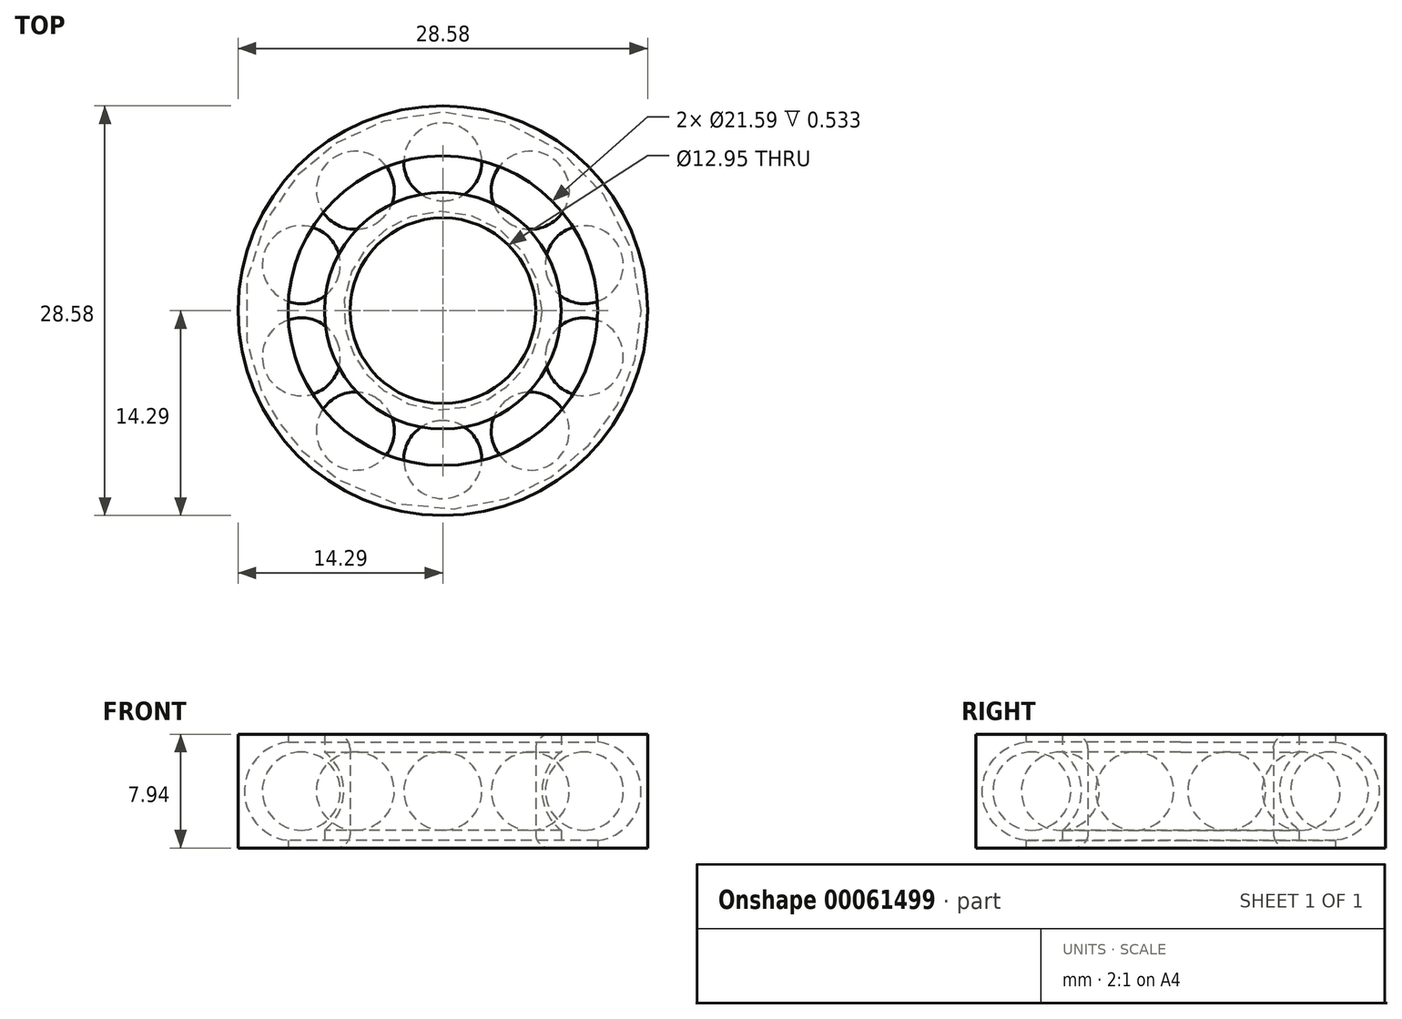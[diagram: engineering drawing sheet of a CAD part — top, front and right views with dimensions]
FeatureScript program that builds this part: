
annotation { "Feature Type Name" : "Feature", "Feature Type Description" : "" }
export const myFeature = defineFeature(function(context is Context, id is Id, definition is map)
    precondition{}
    {
        {
            var Q0;
            Q0=qCreatedBy(makeId("Top.planeOp"),FACE);
            var sketch = newSketch(context, id + "F0", { "sketchPlane" : qUnion([Q0])});
            skCircle(sketch, "E0", {"center": v(0, 0) * mm, "radius": 6.48 * mm});
            skCircle(sketch, "E1", {"center": v(0, 0) * mm, "radius": 14.29 * mm});
            skSolve(sketch);
        }
        {
            var Q0;
            Q0 = qSketchRegion(id + "F0", true);
            extrude(context, id + "F1", {"entities" : qUnion([Q0]), "depth" : 7.94 * mm});
        }
        {
            var Q0;
            Q0=qCreatedBy(makeId("Top.planeOp"),FACE);
            var sketch = newSketch(context, id + "F2", { "sketchPlane" : qUnion([Q0])});
            skCircle(sketch, "E2", {"center": v(0, 0) * mm, "radius": 8.26 * mm});
            skCircle(sketch, "E3", {"center": v(0, 0) * mm, "radius": 10.8 * mm});
            skSolve(sketch);
        }
        {
            var Q0;
            Q0 = qSketchRegion(id + "F2", true);
            extrude(context, id + "F3", {"entities" : qUnion([Q0]), "operationType" : NewBodyOperationType.REMOVE, "endBound" : BoundingType.UP_TO_NEXT, "depth" : 6 * mm});
        }
        {
            var Q0;
            Q0=qCreatedBy(makeId("Right.planeOp"),FACE);
            var sketch = newSketch(context, id + "F4", { "sketchPlane" : qUnion([Q0])});
            skLineSegment(sketch, "E4", {"start": v(10.38, 3.97) * mm, "end": v(10.38, 7.94) * mm, "construction": true});
            skLineSegment(sketch, "E5.0", {"start": v(-6.48, 7.94) * mm, "end": v(6.48, 7.94) * mm, "construction": true});
            skLineSegment(sketch, "E5.1", {"start": v(-14.29, 7.94) * mm, "end": v(14.29, 7.94) * mm, "construction": true});
            skLineSegment(sketch, "E6", {"start": v(6.48, 7.94) * mm, "end": v(14.29, 7.94) * mm, "construction": true});
            skLineSegment(sketch, "E7", {"start": v(14.29, 7.94) * mm, "end": v(14.29, 0) * mm, "construction": true});
            skLineSegment(sketch, "E8", {"start": v(6.48, 7.94) * mm, "end": v(6.48, 0) * mm, "construction": true});
            skLineSegment(sketch, "E9", {"start": v(6.48, 3.97) * mm, "end": v(14.29, 3.97) * mm, "construction": true});
            skLineSegment(sketch, "E10", {"start": v(0, 0) * mm, "end": v(0, 7.94) * mm, "construction": true});
            skCircle(sketch, "E11", {"center": v(10.38, 3.97) * mm, "radius": 3.46 * mm});
            skSolve(sketch);
        }
        {
            var Q0;
            Q0=makeQuery(id+"F4.imprint","IMPRINT",FACE,{"disambiguationData":[TD([[makeQuery(id+"F4.imprint","IMPRINT",EDGE,{"derivedFrom":sQuery(id+"F4.wireOp",EDGE,"E11")}),1.0]])]});
            var Q1;
            Q1=sQuery(id+"F4.wireOp",EDGE,"E10");
            revolve(context, id + "F5", {"operationType" : NewBodyOperationType.REMOVE, "entities" : qUnion([Q0]), "axis" : qUnion([Q1]), "revolveType" : RevolveType.FULL, "oppositeDirection" : true});
        }
        {
            var Q0;
            Q0=qCreatedBy(makeId("Right.planeOp"),FACE);
            var sketch = newSketch(context, id + "F6", { "sketchPlane" : qUnion([Q0])});
            skLineSegment(sketch, "E12.0", {"start": v(-14.29, 7.94) * mm, "end": v(14.29, 7.94) * mm, "construction": true});
            skLineSegment(sketch, "E13", {"start": v(0, 0) * mm, "end": v(0, 7.94) * mm, "construction": true});
            skLineSegment(sketch, "E14.0", {"start": v(-6.48, 7.94) * mm, "end": v(6.48, 7.94) * mm, "construction": true});
            skLineSegment(sketch, "E15", {"start": v(6.48, 7.94) * mm, "end": v(14.29, 7.94) * mm, "construction": true});
            skLineSegment(sketch, "E16", {"start": v(6.48, 7.94) * mm, "end": v(6.48, 0) * mm, "construction": true});
            skLineSegment(sketch, "E17", {"start": v(14.29, 7.94) * mm, "end": v(14.29, 0) * mm, "construction": true});
            skLineSegment(sketch, "E18", {"start": v(10.38, 7.94) * mm, "end": v(10.38, 0) * mm, "construction": true});
            skArc(sketch, "E19", {"start": v(10.38, 6.7) * mm, "mid": v(7.66, 3.97) * mm, "end": v(10.38, 1.25) * mm});
            skLineSegment(sketch, "E20", {"start": v(10.38, 6.7) * mm, "end": v(10.38, 1.25) * mm});
            skSolve(sketch);
        }
        {
            var Q0;
            Q0 = qSketchRegion(id + "F6", true);
            var Q1;
            Q1=sQuery(id+"F4.wireOp",EDGE,"E4");
            revolve(context, id + "F7", {"entities" : qUnion([Q0]), "axis" : qUnion([Q1]), "revolveType" : RevolveType.FULL});
        }
        {
            var Q0;
            Q0=makeQuery(id+"F7.opRevolve","SWEPT_BODY",BODY,{"disambiguationData":[OSD([sQuery(id+"F6.wireOp",EDGE,"E19"),sQuery(id+"F6.wireOp",EDGE,"E20")])]});
            var Q1;
            Q1=sQuery(id+"F4.wireOp",EDGE,"E10");
            circularPattern(context, id + "F8", {"entities" : qUnion([Q0]), "axis" : qUnion([Q1]), "angle" : 360 * degree, "instanceCount" : 10, "equalSpace" : true, "computeTransformsWithoutBuiltin" : true});
        }
        {
            var Q0;
            Q0=makeQuery(id+"F1.opExtrude","CAP_EDGE",EDGE,{"disambiguationData":[OSD([sQuery(id+"F0.wireOp",EDGE,"E0")])],"isStart":true});
            var Q1;
            Q1=makeQuery(id+"F1.opExtrude","CAP_EDGE",EDGE,{"disambiguationData":[OSD([sQuery(id+"F0.wireOp",EDGE,"E0")])],"isStart":false});
            fillet(context, id + "F9", {"entities" : qUnion([Q0, Q1]), "radius" : 1 * mm, "tangentPropagation" : true, "allowEdgeOverflow" : false});
        }
    });
